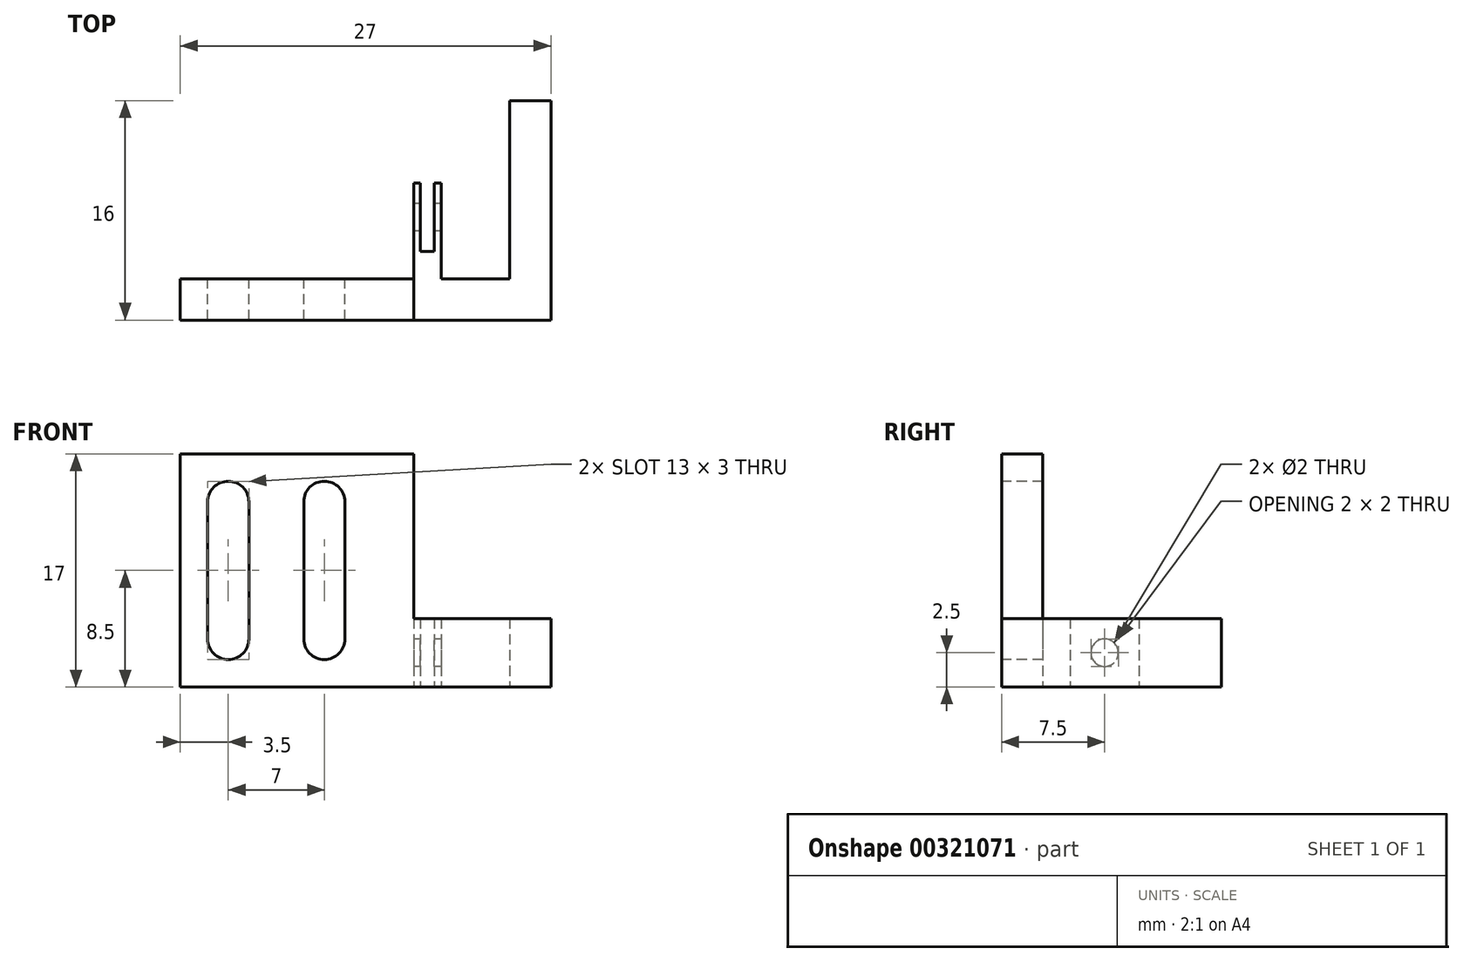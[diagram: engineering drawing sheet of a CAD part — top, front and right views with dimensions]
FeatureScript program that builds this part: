
annotation { "Feature Type Name" : "Feature", "Feature Type Description" : "" }
export const myFeature = defineFeature(function(context is Context, id is Id, definition is map)
    precondition{}
    {
        {
            var Q0;
            Q0=qCreatedBy(makeId("Front.planeOp"),FACE);
            var sketch = newSketch(context, id + "F0", { "sketchPlane" : qUnion([Q0])});
            skLineSegment(sketch, "E0.bottom", {"start": v(8.5, 8.5) * mm, "end": v(-8.5, 8.5) * mm});
            skLineSegment(sketch, "E0.top", {"start": v(8.5, -8.5) * mm, "end": v(-8.5, -8.5) * mm});
            skLineSegment(sketch, "E0.left", {"start": v(8.5, 8.5) * mm, "end": v(8.5, -8.5) * mm});
            skLineSegment(sketch, "E0.right", {"start": v(-8.5, 8.5) * mm, "end": v(-8.5, -8.5) * mm});
            skPoint(sketch, "E0.middle", {"position": v(0, 0) * mm});
            skLineSegment(sketch, "E1.bottom", {"start": v(-3.5, 6.5) * mm, "end": v(-6.5, 6.5) * mm});
            skLineSegment(sketch, "E1.top", {"start": v(-3.5, -6.5) * mm, "end": v(-6.5, -6.5) * mm});
            skLineSegment(sketch, "E1.left", {"start": v(-3.5, 6.5) * mm, "end": v(-3.5, -6.5) * mm});
            skLineSegment(sketch, "E1.right", {"start": v(-6.5, 6.5) * mm, "end": v(-6.5, -6.5) * mm});
            skPoint(sketch, "E1.middle", {"position": v(-5, 0) * mm});
            skLineSegment(sketch, "E2.bottom", {"start": v(3.5, 6.5) * mm, "end": v(0.5, 6.5) * mm});
            skLineSegment(sketch, "E2.top", {"start": v(3.5, -6.5) * mm, "end": v(0.5, -6.5) * mm});
            skLineSegment(sketch, "E2.left", {"start": v(3.5, 6.5) * mm, "end": v(3.5, -6.5) * mm});
            skLineSegment(sketch, "E2.right", {"start": v(0.5, 6.5) * mm, "end": v(0.5, -6.5) * mm});
            skPoint(sketch, "E2.middle", {"position": v(2, 0) * mm});
            skSolve(sketch);
        }
        {
            var Q0;
            Q0 = qSketchRegion(id + "F0", true);
            extrude(context, id + "F1", {"entities" : qUnion([Q0]), "depth" : 3 * mm});
        }
        {
            var Q0;
            Q0=makeQuery(id+"F1.opExtrude","SWEPT_FACE",FACE,{"disambiguationData":[OSD([sQuery(id+"F0.wireOp",EDGE,"E0.left")])]});
            var sketch = newSketch(context, id + "F2", { "sketchPlane" : qUnion([Q0])});
            skLineSegment(sketch, "E3.bottom", {"start": v(-3, -3.5) * mm, "end": v(0, -3.5) * mm});
            skLineSegment(sketch, "E3.top", {"start": v(-3, -8.5) * mm, "end": v(0, -8.5) * mm});
            skLineSegment(sketch, "E3.left", {"start": v(-3, -3.5) * mm, "end": v(-3, -8.5) * mm});
            skLineSegment(sketch, "E3.right", {"start": v(0, -3.5) * mm, "end": v(0, -8.5) * mm});
            skSolve(sketch);
        }
        {
            var Q0;
            Q0 = qSketchRegion(id + "F2", true);
            extrude(context, id + "F3", {"entities" : qUnion([Q0]), "operationType" : NewBodyOperationType.ADD, "depth" : 10 * mm});
        }
        {
            var Q0;
            Q0=makeQuery(id+"F3.boolean.opBoolean","MERGE",FACE,{"derivedFrom":[makeQuery(id+"F1.opExtrude","CAP_FACE",FACE,{"disambiguationData":[OSD([sQuery(id+"F0.wireOp",EDGE,"E0.bottom"),sQuery(id+"F0.wireOp",EDGE,"E0.top"),sQuery(id+"F0.wireOp",EDGE,"E0.left"),sQuery(id+"F0.wireOp",EDGE,"E0.right"),sQuery(id+"F0.wireOp",EDGE,"E1.bottom"),sQuery(id+"F0.wireOp",EDGE,"E1.top"),sQuery(id+"F0.wireOp",EDGE,"E1.left"),sQuery(id+"F0.wireOp",EDGE,"E1.right"),sQuery(id+"F0.wireOp",EDGE,"E2.bottom"),sQuery(id+"F0.wireOp",EDGE,"E2.top"),sQuery(id+"F0.wireOp",EDGE,"E2.left"),sQuery(id+"F0.wireOp",EDGE,"E2.right")])],"isStart":true}),makeQuery(id+"F3.opExtrude","SWEPT_FACE",FACE,{"disambiguationData":[OSD([sQuery(id+"F2.wireOp",EDGE,"E3.right")])]})]});
            var sketch = newSketch(context, id + "F4", { "sketchPlane" : qUnion([Q0])});
            skLineSegment(sketch, "E4.bottom", {"start": v(-18.5, -3.5) * mm, "end": v(-15.5, -3.5) * mm});
            skLineSegment(sketch, "E4.top", {"start": v(-18.5, -8.5) * mm, "end": v(-15.5, -8.5) * mm});
            skLineSegment(sketch, "E4.left", {"start": v(-18.5, -3.5) * mm, "end": v(-18.5, -8.5) * mm});
            skLineSegment(sketch, "E4.right", {"start": v(-15.5, -3.5) * mm, "end": v(-15.5, -8.5) * mm});
            skSolve(sketch);
        }
        {
            var Q0;
            Q0 = qSketchRegion(id + "F4", true);
            extrude(context, id + "F5", {"entities" : qUnion([Q0]), "operationType" : NewBodyOperationType.ADD, "depth" : 13 * mm});
        }
        {
            var Q0;
            Q0=makeQuery(id+"F3.boolean.opBoolean","MERGE",FACE,{"derivedFrom":[makeQuery(id+"F1.opExtrude","CAP_FACE",FACE,{"disambiguationData":[OSD([sQuery(id+"F0.wireOp",EDGE,"E0.bottom"),sQuery(id+"F0.wireOp",EDGE,"E0.top"),sQuery(id+"F0.wireOp",EDGE,"E0.left"),sQuery(id+"F0.wireOp",EDGE,"E0.right"),sQuery(id+"F0.wireOp",EDGE,"E1.bottom"),sQuery(id+"F0.wireOp",EDGE,"E1.top"),sQuery(id+"F0.wireOp",EDGE,"E1.left"),sQuery(id+"F0.wireOp",EDGE,"E1.right"),sQuery(id+"F0.wireOp",EDGE,"E2.bottom"),sQuery(id+"F0.wireOp",EDGE,"E2.top"),sQuery(id+"F0.wireOp",EDGE,"E2.left"),sQuery(id+"F0.wireOp",EDGE,"E2.right")])],"isStart":true}),makeQuery(id+"F3.opExtrude","SWEPT_FACE",FACE,{"disambiguationData":[OSD([sQuery(id+"F2.wireOp",EDGE,"E3.right")])]})]});
            var sketch = newSketch(context, id + "F6", { "sketchPlane" : qUnion([Q0])});
            skLineSegment(sketch, "E5.bottom", {"start": v(-8.5, -3.5) * mm, "end": v(-10.5, -3.5) * mm});
            skLineSegment(sketch, "E5.top", {"start": v(-8.5, -8.5) * mm, "end": v(-10.5, -8.5) * mm});
            skLineSegment(sketch, "E5.left", {"start": v(-8.5, -3.5) * mm, "end": v(-8.5, -8.5) * mm});
            skLineSegment(sketch, "E5.right", {"start": v(-10.5, -3.5) * mm, "end": v(-10.5, -8.5) * mm});
            skSolve(sketch);
        }
        {
            var Q0;
            Q0 = qSketchRegion(id + "F6", true);
            extrude(context, id + "F7", {"entities" : qUnion([Q0]), "operationType" : NewBodyOperationType.ADD, "depth" : 7 * mm});
        }
        {
            var Q0;
            Q0=makeQuery(id+"F7.opExtrude","CAP_FACE",FACE,{"disambiguationData":[OSD([sQuery(id+"F6.wireOp",EDGE,"E5.bottom"),sQuery(id+"F6.wireOp",EDGE,"E5.top"),sQuery(id+"F6.wireOp",EDGE,"E5.left"),sQuery(id+"F6.wireOp",EDGE,"E5.right")])],"isStart":false});
            var sketch = newSketch(context, id + "F8", { "sketchPlane" : qUnion([Q0])});
            skLineSegment(sketch, "E6.bottom", {"start": v(-10, -3.5) * mm, "end": v(-9, -3.5) * mm});
            skLineSegment(sketch, "E6.top", {"start": v(-10, -8.5) * mm, "end": v(-9, -8.5) * mm});
            skLineSegment(sketch, "E6.left", {"start": v(-10, -3.5) * mm, "end": v(-10, -8.5) * mm});
            skLineSegment(sketch, "E6.right", {"start": v(-9, -3.5) * mm, "end": v(-9, -8.5) * mm});
            skSolve(sketch);
        }
        {
            var Q0;
            Q0 = qSketchRegion(id + "F8", true);
            extrude(context, id + "F9", {"entities" : qUnion([Q0]), "operationType" : NewBodyOperationType.REMOVE, "oppositeDirection" : true, "depth" : 5 * mm});
        }
        {
            var Q0;
            Q0=makeQuery(id+"F7.opExtrude","SWEPT_FACE",FACE,{"disambiguationData":[OSD([sQuery(id+"F6.wireOp",EDGE,"E5.left")])]});
            var sketch = newSketch(context, id + "F10", { "sketchPlane" : qUnion([Q0])});
            skCircle(sketch, "E7", {"center": v(-4.5, -6) * mm, "radius": 1 * mm});
            skPoint(sketch, "E7.centerSnap0", {"position": v(-7, -6) * mm});
            skSolve(sketch);
        }
        {
            var Q0;
            Q0 = qSketchRegion(id + "F10", true);
            extrude(context, id + "F11", {"entities" : qUnion([Q0]), "operationType" : NewBodyOperationType.REMOVE, "oppositeDirection" : true, "depth" : 3 * mm});
        }
        {
            var Q0;
            Q0=makeQuery(id+"F1.opExtrude","SWEPT_EDGE",EDGE,{"disambiguationData":[OSD([sQuery(id+"F0.wireOp",EDGE,"E1.bottom"),sQuery(id+"F0.wireOp",EDGE,"E1.right")])]});
            var Q1;
            Q1=makeQuery(id+"F1.opExtrude","SWEPT_EDGE",EDGE,{"disambiguationData":[OSD([sQuery(id+"F0.wireOp",EDGE,"E2.bottom"),sQuery(id+"F0.wireOp",EDGE,"E2.right")])]});
            var Q2;
            Q2=makeQuery(id+"F1.opExtrude","SWEPT_EDGE",EDGE,{"disambiguationData":[OSD([sQuery(id+"F0.wireOp",EDGE,"E2.bottom"),sQuery(id+"F0.wireOp",EDGE,"E2.left")])]});
            var Q3;
            Q3=makeQuery(id+"F1.opExtrude","SWEPT_EDGE",EDGE,{"disambiguationData":[OSD([sQuery(id+"F0.wireOp",EDGE,"E1.bottom"),sQuery(id+"F0.wireOp",EDGE,"E1.left")])]});
            var Q4;
            Q4=makeQuery(id+"F1.opExtrude","SWEPT_EDGE",EDGE,{"disambiguationData":[OSD([sQuery(id+"F0.wireOp",EDGE,"E1.top"),sQuery(id+"F0.wireOp",EDGE,"E1.left")])]});
            var Q5;
            Q5=makeQuery(id+"F1.opExtrude","SWEPT_EDGE",EDGE,{"disambiguationData":[OSD([sQuery(id+"F0.wireOp",EDGE,"E2.top"),sQuery(id+"F0.wireOp",EDGE,"E2.left")])]});
            var Q6;
            Q6=makeQuery(id+"F1.opExtrude","SWEPT_EDGE",EDGE,{"disambiguationData":[OSD([sQuery(id+"F0.wireOp",EDGE,"E2.top"),sQuery(id+"F0.wireOp",EDGE,"E2.right")])]});
            var Q7;
            Q7=makeQuery(id+"F1.opExtrude","SWEPT_EDGE",EDGE,{"disambiguationData":[OSD([sQuery(id+"F0.wireOp",EDGE,"E1.top"),sQuery(id+"F0.wireOp",EDGE,"E1.right")])]});
            fillet(context, id + "F12", {"entities" : qUnion([Q0, Q1, Q2, Q3, Q4, Q5, Q6, Q7]), "radius" : 1.5 * mm, "tangentPropagation" : true, "allowEdgeOverflow" : false});
        }
    });
